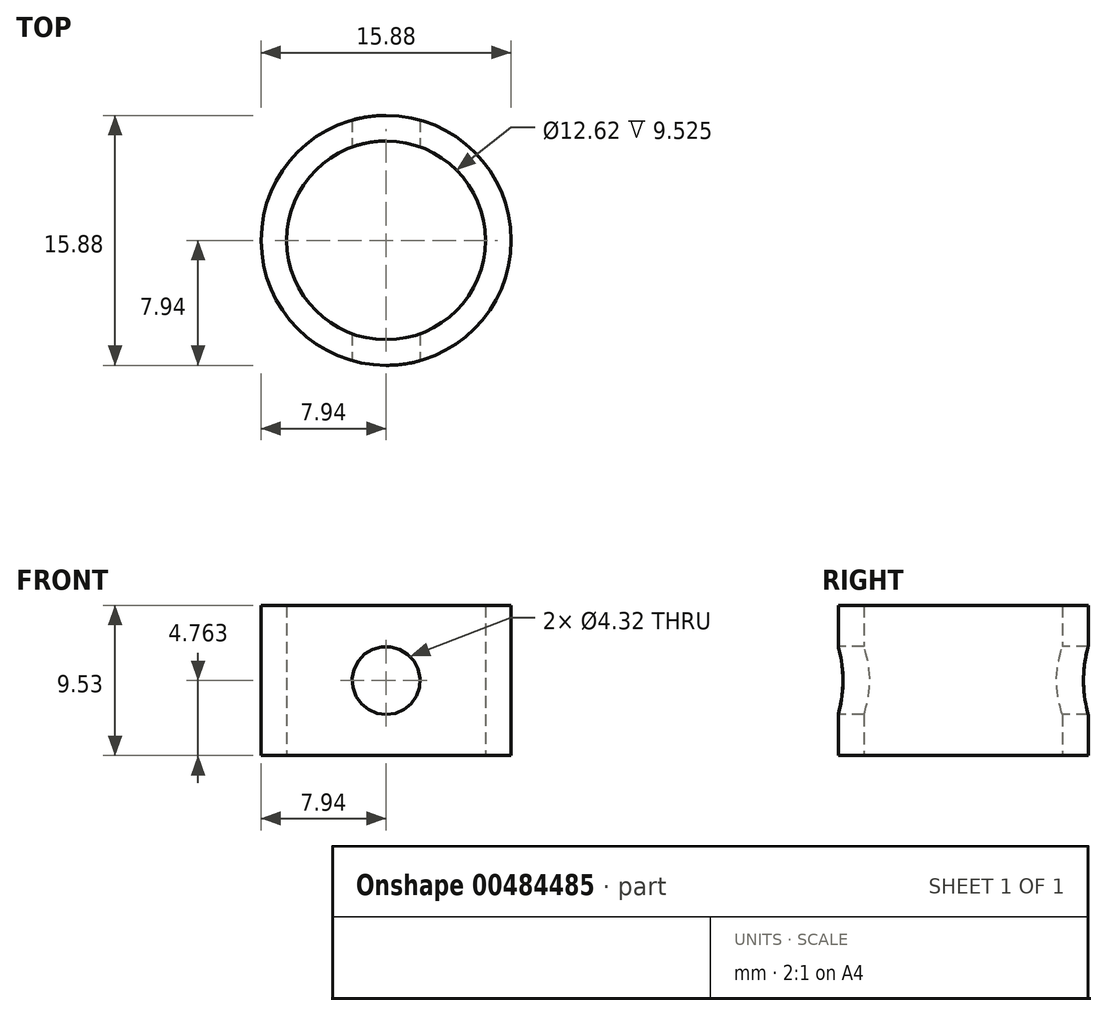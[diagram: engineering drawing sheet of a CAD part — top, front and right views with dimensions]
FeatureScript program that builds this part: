
annotation { "Feature Type Name" : "Feature", "Feature Type Description" : "" }
export const myFeature = defineFeature(function(context is Context, id is Id, definition is map)
    precondition{}
    {
        {
            var Q0;
            Q0=qCreatedBy(makeId("Top.planeOp"),FACE);
            var sketch = newSketch(context, id + "F0", { "sketchPlane" : qUnion([Q0])});
            skCircle(sketch, "E0", {"center": v(0, 0) * mm, "radius": 7.94 * mm});
            skCircle(sketch, "E1", {"center": v(0, 0) * mm, "radius": 6.31 * mm});
            skSolve(sketch);
        }
        {
            var Q0;
            Q0 = qSketchRegion(id + "F0", true);
            extrude(context, id + "F1", {"entities" : qUnion([Q0]), "depth" : 9.52 * mm, "offsetDistance" : 25.4 * mm});
        }
        {
            var Q0;
            Q0=qCreatedBy(makeId("Front.planeOp"),FACE);
            var sketch = newSketch(context, id + "F2", { "sketchPlane" : qUnion([Q0])});
            skCircle(sketch, "E2", {"center": v(0, 4.76) * mm, "radius": 2.16 * mm});
            skSolve(sketch);
        }
        {
            var Q0;
            Q0 = qSketchRegion(id + "F2", true);
            extrude(context, id + "F3", {"entities" : qUnion([Q0]), "operationType" : NewBodyOperationType.REMOVE, "oppositeDirection" : true, "depth" : 25.4 * mm, "offsetDistance" : 25.4 * mm, "hasSecondDirection" : true, "secondDirectionOppositeDirection" : false, "secondDirectionDepth" : 25.4 * mm});
        }
    });
